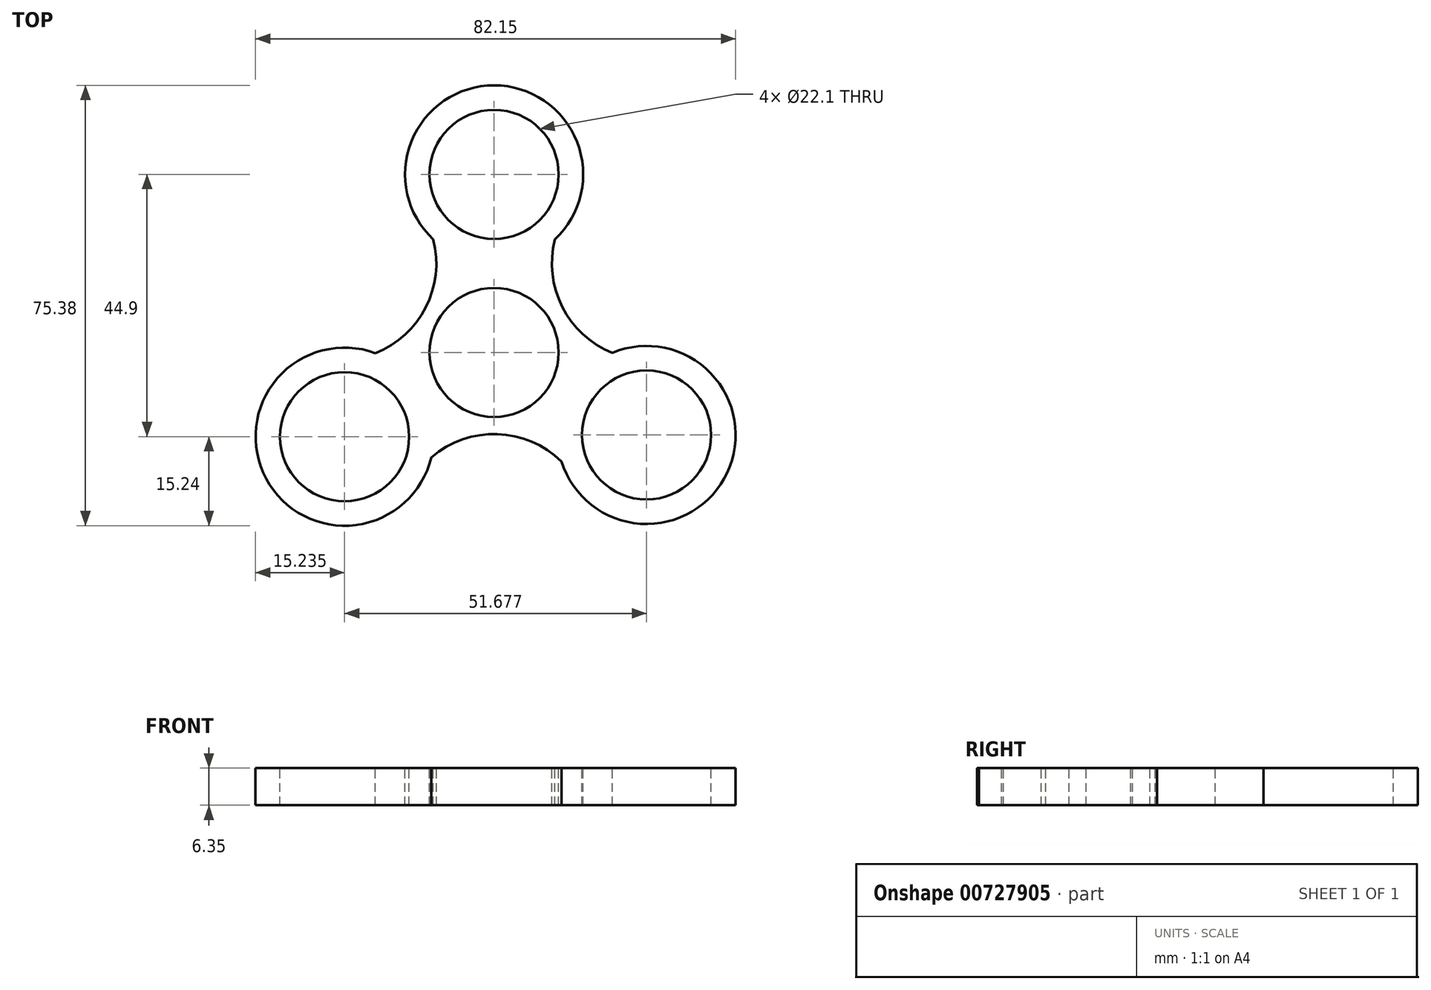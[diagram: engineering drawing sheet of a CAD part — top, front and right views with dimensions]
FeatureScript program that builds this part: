
annotation { "Feature Type Name" : "Feature", "Feature Type Description" : "" }
export const myFeature = defineFeature(function(context is Context, id is Id, definition is map)
    precondition{}
    {
        {
            var Q0;
            Q0=qCreatedBy(makeId("Top.planeOp"),FACE);
            var sketch = newSketch(context, id + "F0", { "sketchPlane" : qUnion([Q0])});
            skCircle(sketch, "E0", {"center": v(0, 0) * mm, "radius": 11.05 * mm});
            skLineSegment(sketch, "E1", {"start": v(0, 0) * mm, "end": v(0, 11.05) * mm});
            skCircle(sketch, "E2", {"center": v(0, 30.48) * mm, "radius": 11.05 * mm});
            skArc(sketch, "E3", {"start": v(10.4, 19.34) * mm, "mid": v(0, 45.72) * mm, "end": v(-10.4, 19.34) * mm});
            skCircle(sketch, "E4.1.0", {"center": v(-25.58, -14.42) * mm, "radius": 11.05 * mm});
            skArc(sketch, "E4.1.1", {"start": v(-20.33, -0.11) * mm, "mid": v(-39.02, -21.62) * mm, "end": v(-10.76, -17.96) * mm});
            skCircle(sketch, "E4.2.0", {"center": v(26.1, -14.13) * mm, "radius": 11.05 * mm});
            skArc(sketch, "E4.2.1", {"start": v(11.55, -18.68) * mm, "mid": v(39.9, -20.56) * mm, "end": v(20.21, -0.07) * mm});
            skPoint(sketch, "E4.center", {"position": v(0.17, 0.64) * mm});
            skArc(sketch, "E5", {"start": v(-20.33, -0.11) * mm, "mid": v(-11.69, 7.74) * mm, "end": v(-10.4, 19.34) * mm});
            skArc(sketch, "E6.1.0", {"start": v(11.55, -18.68) * mm, "mid": v(0.53, -13.98) * mm, "end": v(-10.76, -17.96) * mm});
            skArc(sketch, "E6.2.0", {"start": v(10.4, 19.34) * mm, "mid": v(11.66, 7.8) * mm, "end": v(20.21, -0.07) * mm});
            skLineSegment(sketch, "E7.trimOffspring", {"start": v(0, 15.24) * mm, "end": v(0, 19.43) * mm});
            skSolve(sketch);
        }
        {
            var Q0;
            Q0 = qSketchRegion(id + "F0", true);
            extrude(context, id + "F1", {"entities" : qUnion([Q0]), "oppositeDirection" : true, "depth" : 6.35 * mm, "offsetDistance" : 25.4 * mm});
        }
    });
